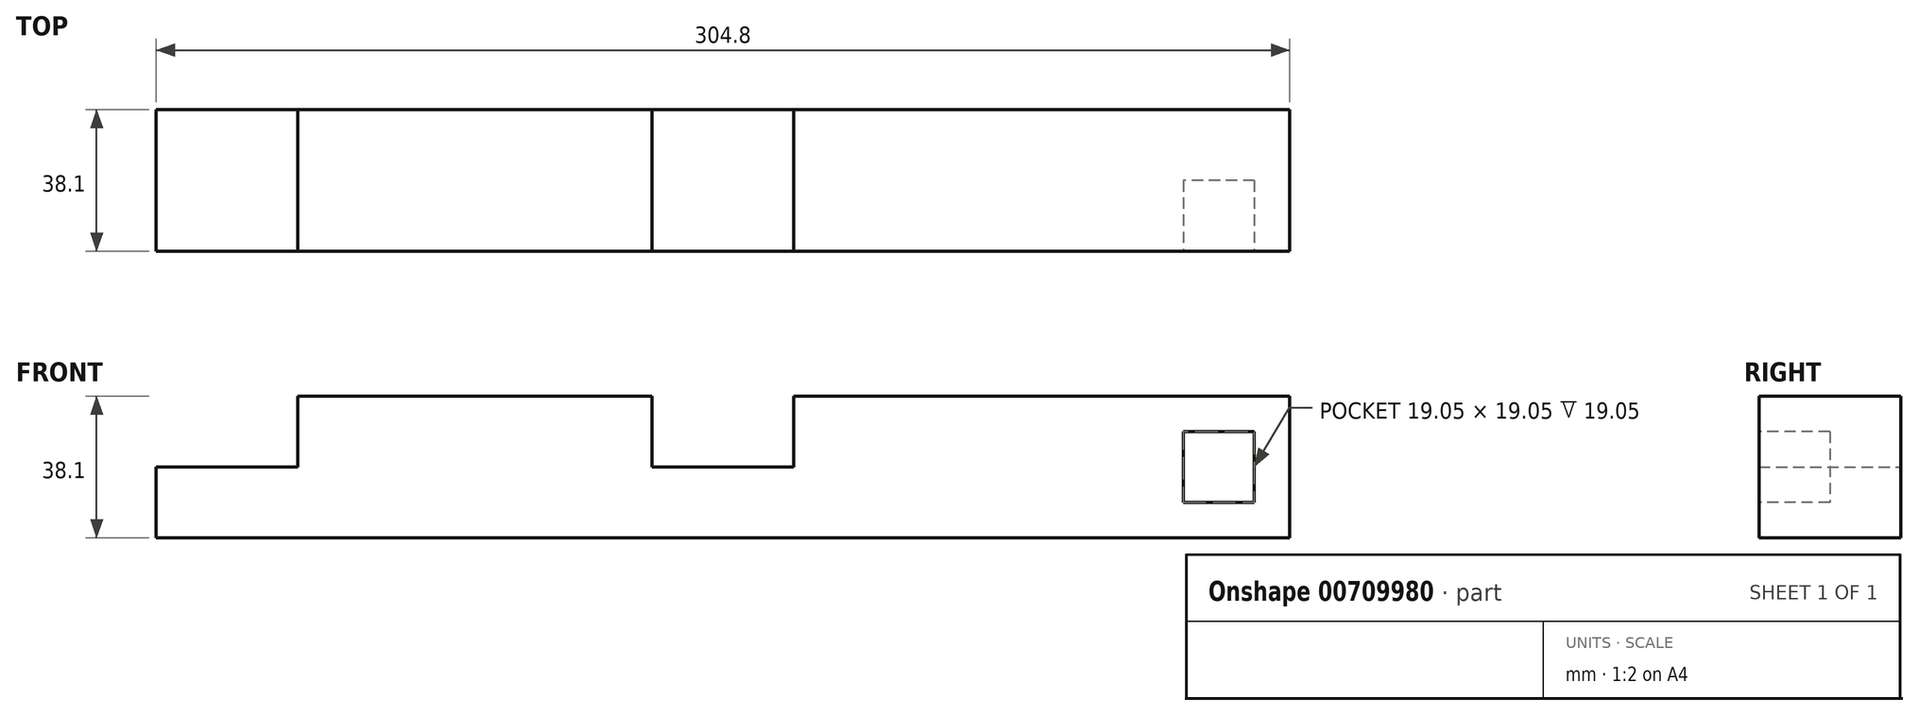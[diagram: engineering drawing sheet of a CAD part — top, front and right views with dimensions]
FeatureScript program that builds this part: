
annotation { "Feature Type Name" : "Feature", "Feature Type Description" : "" }
export const myFeature = defineFeature(function(context is Context, id is Id, definition is map)
    precondition{}
    {
        {
            var Q0;
            Q0=qCreatedBy(makeId("Top.planeOp"),FACE);
            var sketch = newSketch(context, id + "F0", { "sketchPlane" : qUnion([Q0])});
            skLineSegment(sketch, "E0.bottom", {"start": v(152.4, 19.05) * mm, "end": v(-152.4, 19.05) * mm});
            skLineSegment(sketch, "E0.top", {"start": v(152.4, -19.05) * mm, "end": v(-152.4, -19.05) * mm});
            skLineSegment(sketch, "E0.left", {"start": v(152.4, 19.05) * mm, "end": v(152.4, -19.05) * mm});
            skPoint(sketch, "E0.middle", {"position": v(0, 0) * mm});
            skPoint(sketch, "E1", {"position": v(-152.4, 19.05) * mm});
            skLineSegment(sketch, "E2", {"start": v(-152.4, -19.05) * mm, "end": v(-152.4, 19.05) * mm});
            skSolve(sketch);
        }
        {
            var Q0;
            Q0 = qSketchRegion(id + "F0", true);
            extrude(context, id + "F1", {"entities" : qUnion([Q0]), "endBound" : BoundingType.SYMMETRIC, "depth" : 38.1 * mm, "offsetDistance" : 25.4 * mm});
        }
        {
            var Q0;
            Q0=qCreatedBy(makeId("Top.planeOp"),FACE);
            var sketch = newSketch(context, id + "F2", { "sketchPlane" : qUnion([Q0])});
            skLineSegment(sketch, "E3.bottom", {"start": v(19.05, 19.05) * mm, "end": v(-19.05, 19.05) * mm});
            skLineSegment(sketch, "E3.top", {"start": v(19.05, -19.05) * mm, "end": v(-19.05, -19.05) * mm});
            skLineSegment(sketch, "E3.left", {"start": v(19.05, 19.05) * mm, "end": v(19.05, -19.05) * mm});
            skLineSegment(sketch, "E3.right", {"start": v(-19.05, 19.05) * mm, "end": v(-19.05, -19.05) * mm});
            skPoint(sketch, "E3.middle", {"position": v(0, 0) * mm});
            skSolve(sketch);
        }
        {
            var Q0;
            Q0 = qSketchRegion(id + "F2", true);
            extrude(context, id + "F3", {"entities" : qUnion([Q0]), "operationType" : NewBodyOperationType.REMOVE, "depth" : 19.05 * mm, "offsetDistance" : 25.4 * mm});
        }
        {
            var Q0;
            Q0=makeQuery(id+"F1.opExtrude","SWEPT_FACE",FACE,{"disambiguationData":[OSD([sQuery(id+"F0.wireOp",EDGE,"E0.top")])]});
            var sketch = newSketch(context, id + "F4", { "sketchPlane" : qUnion([Q0])});
            skLineSegment(sketch, "E4.bottom", {"start": v(142.88, 9.53) * mm, "end": v(123.82, 9.53) * mm});
            skLineSegment(sketch, "E4.top", {"start": v(142.88, -9.52) * mm, "end": v(123.82, -9.52) * mm});
            skLineSegment(sketch, "E4.left", {"start": v(142.88, 9.53) * mm, "end": v(142.88, -9.52) * mm});
            skLineSegment(sketch, "E4.right", {"start": v(123.82, 9.53) * mm, "end": v(123.82, -9.52) * mm});
            skPoint(sketch, "E4.middle", {"position": v(133.35, 0) * mm});
            skSolve(sketch);
        }
        {
            var Q0;
            Q0 = qSketchRegion(id + "F4", true);
            extrude(context, id + "F5", {"entities" : qUnion([Q0]), "operationType" : NewBodyOperationType.REMOVE, "oppositeDirection" : true, "depth" : 19.05 * mm, "offsetDistance" : 25.4 * mm});
        }
        {
            var Q0;
            {var subQ0=sQuery(id+"F0.wireOp",EDGE,"E0.bottom");var subQ1=sQuery(id+"F0.wireOp",EDGE,"E2");var subQ2=sQuery(id+"F0.wireOp",EDGE,"E0.top");Q0=makeQuery(id+"F3.boolean.opBoolean","SPLIT",FACE,{"disambiguationData":[TD([makeQuery(id+"F1.opExtrude","SWEPT_FACE",FACE,{"disambiguationData":[OSD([subQ1])]})])],"derivedFrom":makeQuery(id+"F1.opExtrude","CAP_FACE",FACE,{"disambiguationData":[OSD([subQ0,subQ2,sQuery(id+"F0.wireOp",EDGE,"E0.left"),subQ1])],"isStart":false})});}
            var sketch = newSketch(context, id + "F6", { "sketchPlane" : qUnion([Q0])});
            skLineSegment(sketch, "E5.bottom", {"start": v(-152.4, 19.05) * mm, "end": v(-114.3, 19.05) * mm});
            skLineSegment(sketch, "E5.top", {"start": v(-152.4, -19.05) * mm, "end": v(-114.3, -19.05) * mm});
            skLineSegment(sketch, "E5.left", {"start": v(-152.4, 19.05) * mm, "end": v(-152.4, -19.05) * mm});
            skLineSegment(sketch, "E5.right", {"start": v(-114.3, 19.05) * mm, "end": v(-114.3, -19.05) * mm});
            skSolve(sketch);
        }
        {
            var Q0;
            Q0 = qSketchRegion(id + "F6", true);
            extrude(context, id + "F7", {"entities" : qUnion([Q0]), "operationType" : NewBodyOperationType.REMOVE, "oppositeDirection" : true, "depth" : 19.05 * mm, "offsetDistance" : 25.4 * mm});
        }
    });
